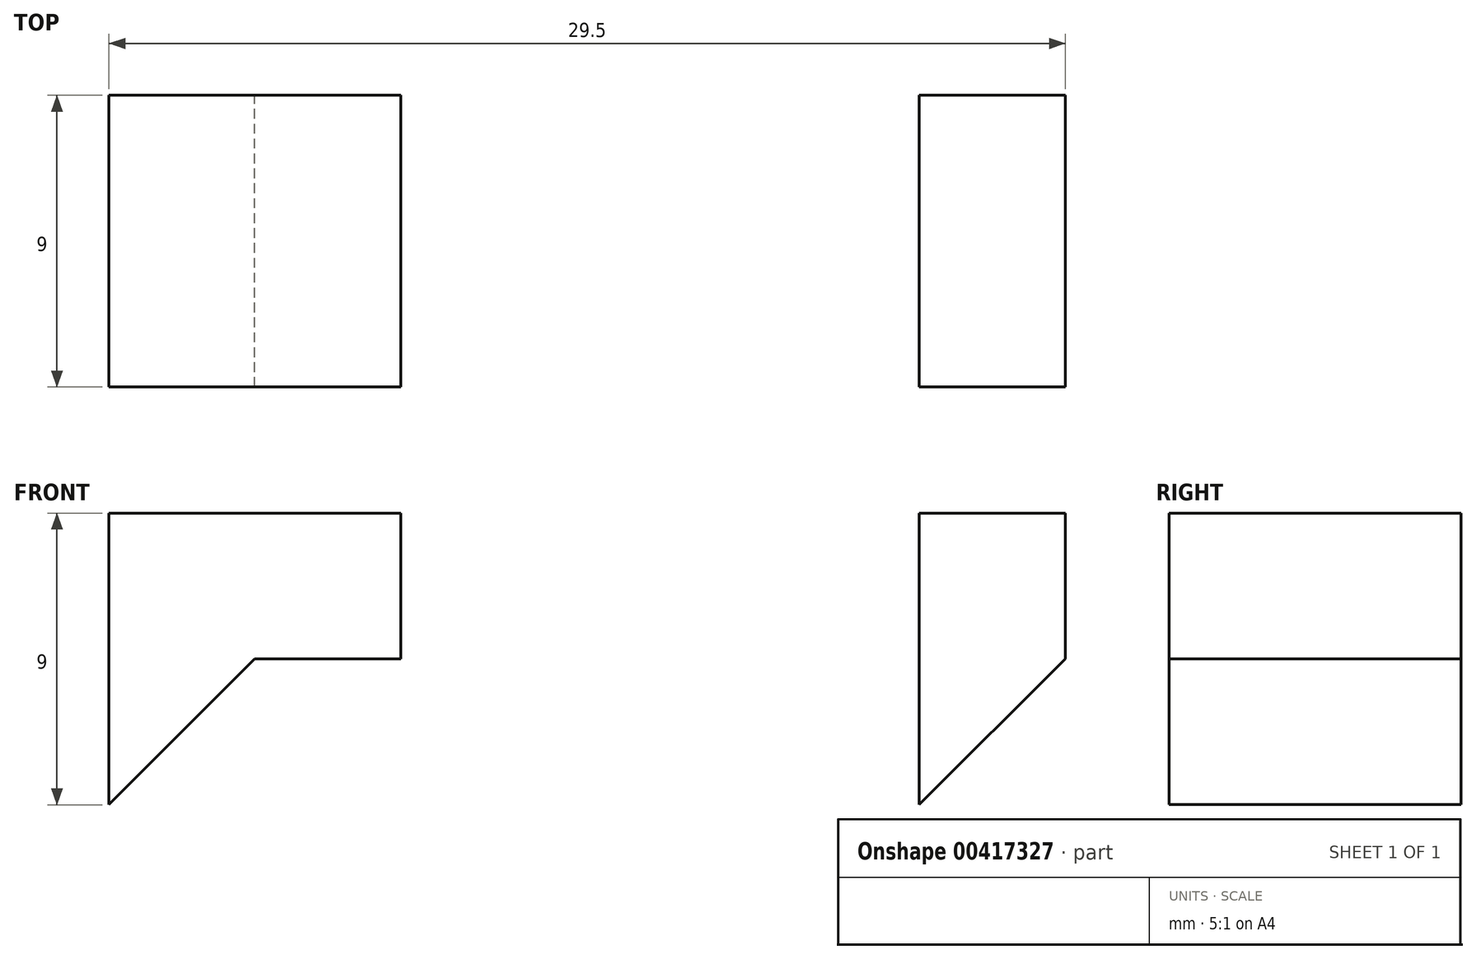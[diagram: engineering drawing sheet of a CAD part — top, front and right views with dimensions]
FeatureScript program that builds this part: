
annotation { "Feature Type Name" : "Feature", "Feature Type Description" : "" }
export const myFeature = defineFeature(function(context is Context, id is Id, definition is map)
    precondition{}
    {
        {
            var Q0;
            Q0=qCreatedBy(makeId("Front.planeOp"),FACE);
            var sketch = newSketch(context, id + "F0", { "sketchPlane" : qUnion([Q0])});
            skLineSegment(sketch, "E0", {"start": v(-0.53, 13.51) * mm, "end": v(-9.53, 13.51) * mm});
            skLineSegment(sketch, "E1", {"start": v(-9.53, 13.51) * mm, "end": v(-9.53, 4.51) * mm});
            skLineSegment(sketch, "E2", {"start": v(-0.53, 13.51) * mm, "end": v(-0.53, 9.01) * mm});
            skLineSegment(sketch, "E3", {"start": v(-0.53, 9.01) * mm, "end": v(-5.03, 9.01) * mm});
            skLineSegment(sketch, "E4", {"start": v(-5.03, 9.01) * mm, "end": v(-9.53, 4.51) * mm});
            skLineSegment(sketch, "E5", {"start": v(-0.53, 13.51) * mm, "end": v(15.47, 13.51) * mm, "construction": true});
            skLineSegment(sketch, "E6", {"start": v(15.47, 13.51) * mm, "end": v(19.97, 13.51) * mm});
            skLineSegment(sketch, "E7", {"start": v(15.47, 13.51) * mm, "end": v(15.47, 4.51) * mm});
            skLineSegment(sketch, "E8", {"start": v(19.97, 13.51) * mm, "end": v(19.97, 9.01) * mm});
            skLineSegment(sketch, "E9", {"start": v(19.97, 9.01) * mm, "end": v(15.47, 4.51) * mm});
            skSolve(sketch);
        }
        {
            var Q0;
            Q0=makeQuery(id+"F0.imprint","IMPRINT",FACE,{"disambiguationData":[TD([[makeQuery(id+"F0.imprint","IMPRINT",EDGE,{"derivedFrom":sQuery(id+"F0.wireOp",EDGE,"E0")}),1.0]])]});
            var Q1;
            Q1=makeQuery(id+"F0.imprint","IMPRINT",FACE,{"disambiguationData":[TD([[makeQuery(id+"F0.imprint","IMPRINT",EDGE,{"derivedFrom":sQuery(id+"F0.wireOp",EDGE,"E6")}),-1.0]])]});
            extrude(context, id + "F1", {"entities" : qUnion([Q0, Q1]), "depth" : 9 * mm, "offsetDistance" : 25 * mm});
        }
    });
